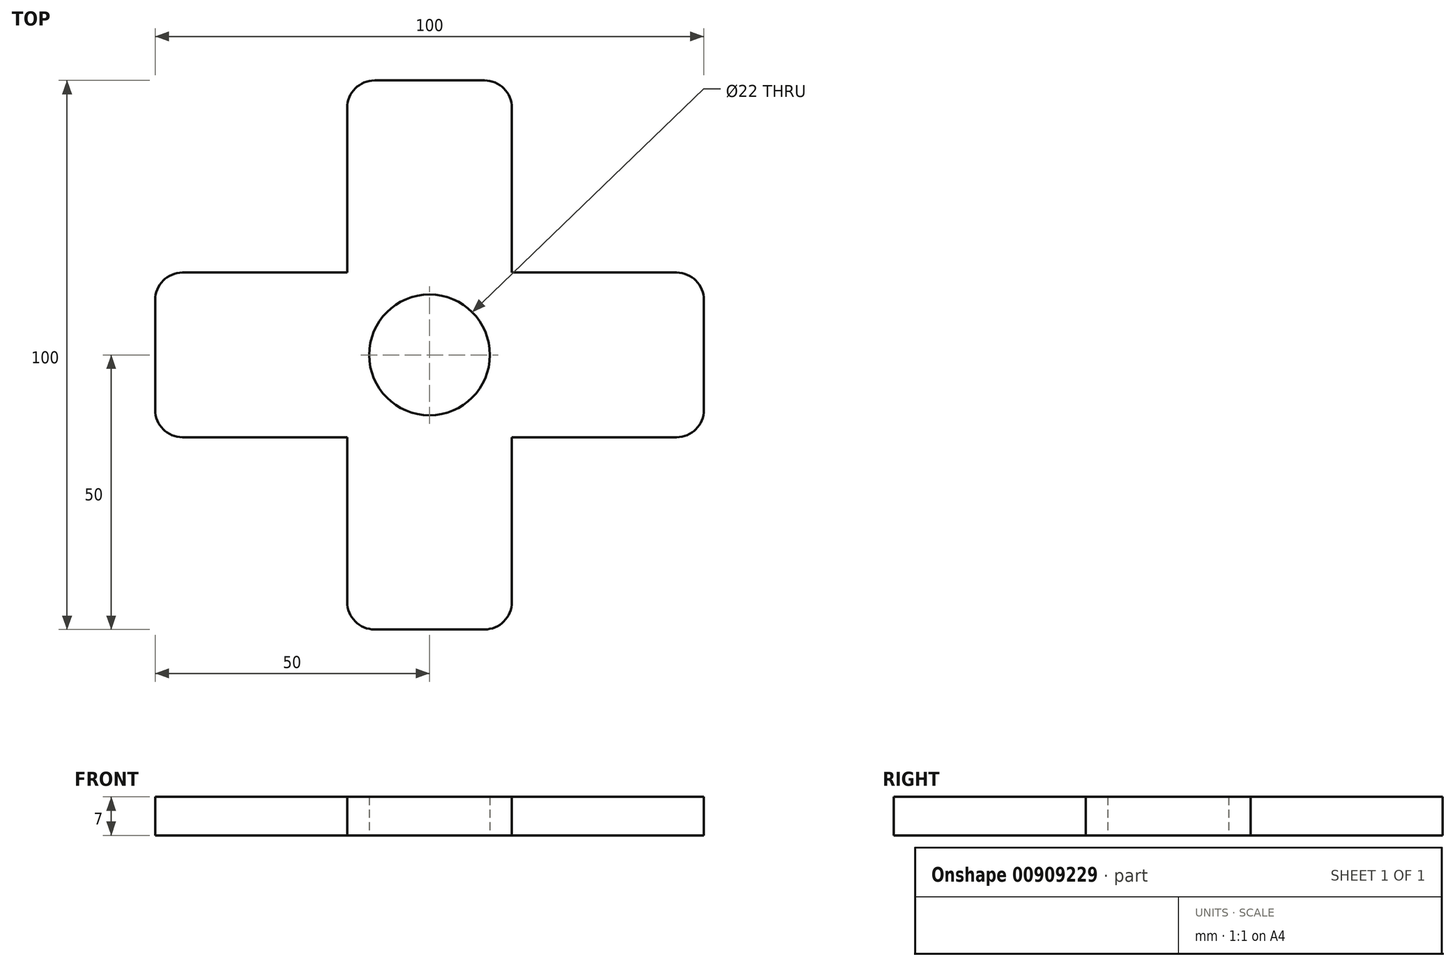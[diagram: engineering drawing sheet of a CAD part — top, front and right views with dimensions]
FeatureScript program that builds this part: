
annotation { "Feature Type Name" : "Feature", "Feature Type Description" : "" }
export const myFeature = defineFeature(function(context is Context, id is Id, definition is map)
    precondition{}
    {
        {
            var Q0;
            Q0=qCreatedBy(makeId("Top.planeOp"),FACE);
            var sketch = newSketch(context, id + "F0", { "sketchPlane" : qUnion([Q0])});
            skCircle(sketch, "E0", {"center": v(0, 0) * mm, "radius": 11 * mm});
            skLineSegment(sketch, "E1.bottom", {"start": v(45, -15) * mm, "end": v(-45, -15) * mm});
            skLineSegment(sketch, "E1.top", {"start": v(45, 15) * mm, "end": v(-45, 15) * mm});
            skLineSegment(sketch, "E1.left", {"start": v(50, -10) * mm, "end": v(50, 10) * mm});
            skLineSegment(sketch, "E1.right", {"start": v(-50, -10) * mm, "end": v(-50, 10) * mm});
            skPoint(sketch, "E2.visualSharp", {"position": v(-50, 15) * mm});
            skArc(sketch, "E2.filletArc", {"start": v(-45, 15) * mm, "mid": v(-48.54, 13.54) * mm, "end": v(-50, 10) * mm});
            skPoint(sketch, "E3.visualSharp", {"position": v(-50, -15) * mm});
            skArc(sketch, "E3.filletArc", {"start": v(-50, -10) * mm, "mid": v(-48.54, -13.54) * mm, "end": v(-45, -15) * mm});
            skPoint(sketch, "E4.visualSharp", {"position": v(50, -15) * mm});
            skArc(sketch, "E4.filletArc", {"start": v(45, -15) * mm, "mid": v(48.54, -13.54) * mm, "end": v(50, -10) * mm});
            skPoint(sketch, "E5.visualSharp", {"position": v(50, 15) * mm});
            skArc(sketch, "E5.filletArc", {"start": v(50, 10) * mm, "mid": v(48.54, 13.54) * mm, "end": v(45, 15) * mm});
            skSolve(sketch);
        }
        {
            var Q0;
            Q0=makeQuery(id+"F0.imprint","IMPRINT",FACE,{"disambiguationData":[TD([[makeQuery(id+"F0.imprint","IMPRINT",EDGE,{"derivedFrom":sQuery(id+"F0.wireOp",EDGE,"E0")}),-1.0]])]});
            extrude(context, id + "F1", {"entities" : qUnion([Q0]), "depth" : 7 * mm, "offsetDistance" : 25 * mm});
        }
        {
            var Q0;
            Q0=makeQuery(id+"F1.opExtrude","SWEPT_BODY",BODY,{"disambiguationData":[OSD([sQuery(id+"F0.wireOp",EDGE,"E0"),sQuery(id+"F0.wireOp",EDGE,"E1.bottom"),sQuery(id+"F0.wireOp",EDGE,"E1.top"),sQuery(id+"F0.wireOp",EDGE,"E1.left"),sQuery(id+"F0.wireOp",EDGE,"E1.right"),sQuery(id+"F0.wireOp",EDGE,"E2.filletArc"),sQuery(id+"F0.wireOp",EDGE,"E3.filletArc"),sQuery(id+"F0.wireOp",EDGE,"E4.filletArc"),sQuery(id+"F0.wireOp",EDGE,"E5.filletArc")])]});
            var Q1;
            Q1=sQuery(id+"F0.wireOp",EDGE,"E0");
            circularPattern(context, id + "F2", {"operationType" : NewBodyOperationType.ADD, "entities" : qUnion([Q0]), "axis" : qUnion([Q1]), "angle" : 360 * degree, "instanceCount" : 4, "equalSpace" : true});
        }
    });
